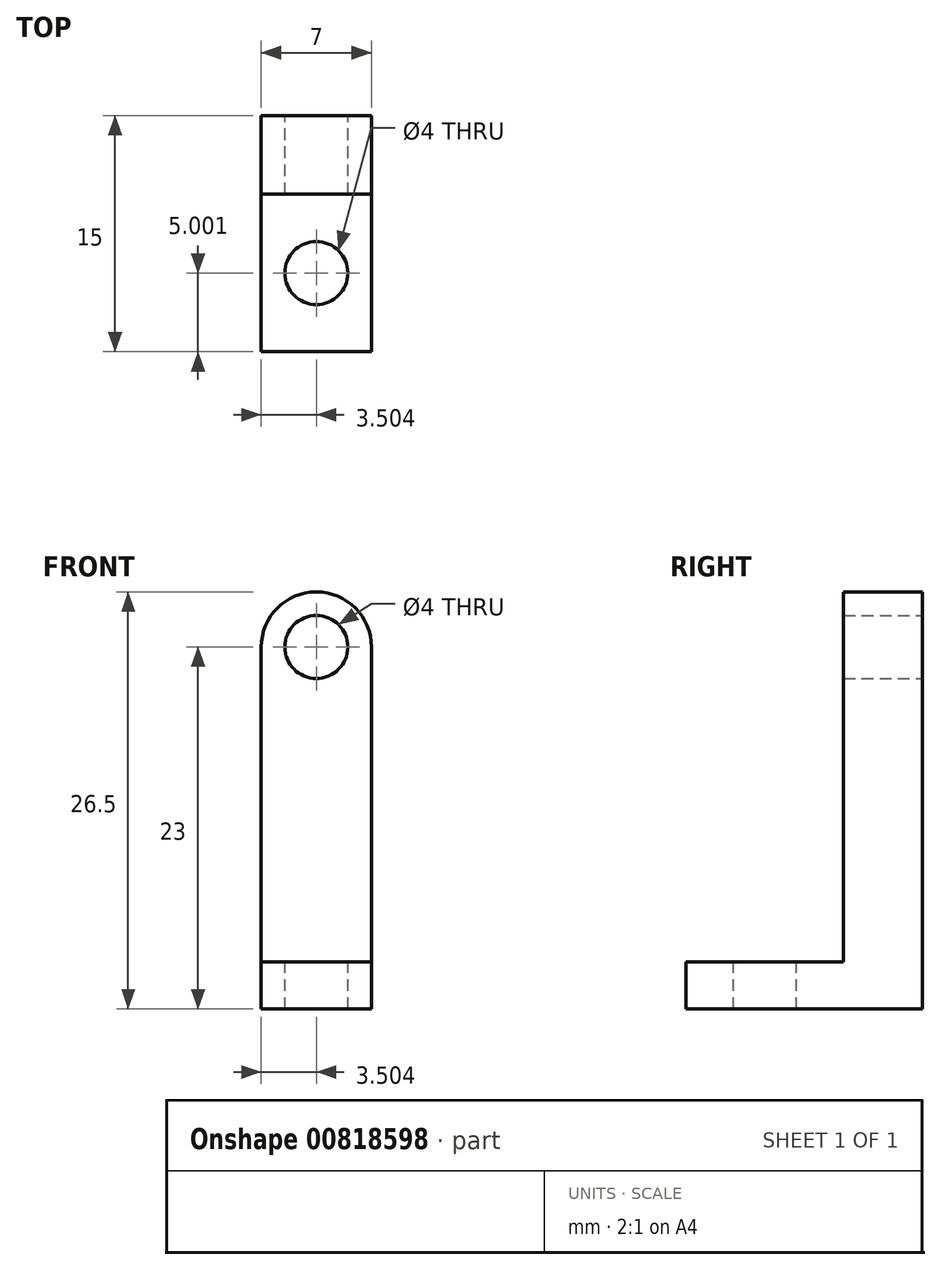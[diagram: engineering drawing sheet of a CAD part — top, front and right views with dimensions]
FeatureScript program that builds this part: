
annotation { "Feature Type Name" : "Feature", "Feature Type Description" : "" }
export const myFeature = defineFeature(function(context is Context, id is Id, definition is map)
    precondition{}
    {
        {
            var Q0;
            Q0=qCreatedBy(makeId("Top.planeOp"),FACE);
            var sketch = newSketch(context, id + "F0", { "sketchPlane" : qUnion([Q0])});
            skLineSegment(sketch, "E0.bottom", {"start": v(-8.2, 9.06) * mm, "end": v(-1.2, 9.06) * mm});
            skLineSegment(sketch, "E0.top", {"start": v(-8.2, -0.94) * mm, "end": v(-1.2, -0.94) * mm});
            skLineSegment(sketch, "E0.left", {"start": v(-8.2, 9.06) * mm, "end": v(-8.2, -0.94) * mm});
            skLineSegment(sketch, "E0.right", {"start": v(-1.2, 9.06) * mm, "end": v(-1.2, -0.94) * mm});
            skLineSegment(sketch, "E1.top", {"start": v(-8.2, 14.06) * mm, "end": v(-1.2, 14.06) * mm});
            skLineSegment(sketch, "E1.left", {"start": v(-8.2, 9.06) * mm, "end": v(-8.2, 14.06) * mm});
            skLineSegment(sketch, "E1.right", {"start": v(-1.2, 9.06) * mm, "end": v(-1.2, 14.06) * mm});
            skSolve(sketch);
        }
        {
            var Q0;
            Q0 = qSketchRegion(id + "F0", true);
            extrude(context, id + "F1", {"entities" : qUnion([Q0]), "depth" : 3 * mm, "offsetDistance" : 25 * mm});
        }
        {
            var Q0;
            Q0=makeQuery(id+"F1.opExtrude","CAP_FACE",FACE,{"disambiguationData":[OSD([sQuery(id+"F0.wireOp",EDGE,"E0.top"),sQuery(id+"F0.wireOp",EDGE,"E0.left"),sQuery(id+"F0.wireOp",EDGE,"E0.right"),sQuery(id+"F0.wireOp",EDGE,"E1.top"),sQuery(id+"F0.wireOp",EDGE,"E1.left"),sQuery(id+"F0.wireOp",EDGE,"E1.right")])],"isStart":false});
            var sketch = newSketch(context, id + "F2", { "sketchPlane" : qUnion([Q0])});
            skLineSegment(sketch, "E2.0", {"start": v(-8.2, 9.06) * mm, "end": v(-1.2, 9.06) * mm});
            skLineSegment(sketch, "E3.0", {"start": v(-8.2, 14.06) * mm, "end": v(-8.2, 9.06) * mm});
            skLineSegment(sketch, "E4.0", {"start": v(-8.2, 14.06) * mm, "end": v(-1.2, 14.06) * mm});
            skLineSegment(sketch, "E5.0", {"start": v(-1.2, 14.06) * mm, "end": v(-1.2, 9.06) * mm});
            skPoint(sketch, "E6.orphan", {"position": v(-8.2, -0.94) * mm});
            skPoint(sketch, "E7.orphan", {"position": v(-1.2, -0.94) * mm});
            skSolve(sketch);
        }
        {
            var Q0;
            Q0 = qSketchRegion(id + "F2", true);
            extrude(context, id + "F3", {"entities" : qUnion([Q0]), "operationType" : NewBodyOperationType.ADD, "depth" : 20 * mm, "offsetDistance" : 25 * mm});
        }
        {
            var Q0;
            Q0=makeQuery(id+"F3.boolean.opBoolean","MERGE",FACE,{"derivedFrom":[makeQuery(id+"F1.opExtrude","SWEPT_FACE",FACE,{"disambiguationData":[OSD([sQuery(id+"F0.wireOp",EDGE,"E1.top")])]}),makeQuery(id+"F3.opExtrude","SWEPT_FACE",FACE,{"disambiguationData":[OSD([sQuery(id+"F2.wireOp",EDGE,"E4.0")])]})]});
            var sketch = newSketch(context, id + "F4", { "sketchPlane" : qUnion([Q0])});
            skLineSegment(sketch, "E8.0", {"start": v(8.2, 23) * mm, "end": v(1.2, 23) * mm});
            skPoint(sketch, "E9", {"position": v(4.7, 23) * mm});
            skArc(sketch, "E10", {"start": v(8.2, 23) * mm, "mid": v(4.7, 26.5) * mm, "end": v(1.2, 23) * mm});
            skSolve(sketch);
        }
        {
            var Q0;
            Q0 = qSketchRegion(id + "F4", true);
            var Q1;
            Q1=makeQuery(id+"F3.opExtrude","SWEPT_FACE",FACE,{"disambiguationData":[OSD([sQuery(id+"F2.wireOp",EDGE,"E2.0")])]});
            extrude(context, id + "F5", {"entities" : qUnion([Q0]), "operationType" : NewBodyOperationType.ADD, "endBound" : BoundingType.UP_TO_SURFACE, "oppositeDirection" : true, "depth" : 25 * mm, "endBoundEntityFace" : qUnion([Q1]), "offsetDistance" : 25 * mm});
        }
        {
            var Q0;
            Q0=makeQuery(id+"F5.boolean.opBoolean","MERGE",FACE,{"derivedFrom":[makeQuery(id+"F3.boolean.opBoolean","MERGE",FACE,{"derivedFrom":[makeQuery(id+"F1.opExtrude","SWEPT_FACE",FACE,{"disambiguationData":[OSD([sQuery(id+"F0.wireOp",EDGE,"E1.top")])]}),makeQuery(id+"F3.opExtrude","SWEPT_FACE",FACE,{"disambiguationData":[OSD([sQuery(id+"F2.wireOp",EDGE,"E4.0")])]})]}),makeQuery(id+"F5.opExtrude","CAP_FACE",FACE,{"disambiguationData":[OSD([sQuery(id+"F4.wireOp",EDGE,"E8.0"),sQuery(id+"F4.wireOp",EDGE,"E10")])],"isStart":true})]});
            var sketch = newSketch(context, id + "F6", { "sketchPlane" : qUnion([Q0])});
            skLineSegment(sketch, "E11", {"start": v(1.2, 23) * mm, "end": v(8.2, 23) * mm, "construction": true});
            skCircle(sketch, "E12", {"center": v(4.7, 23) * mm, "radius": 2 * mm});
            skSolve(sketch);
        }
        {
            var Q0;
            Q0 = qSketchRegion(id + "F6", true);
            extrude(context, id + "F7", {"entities" : qUnion([Q0]), "operationType" : NewBodyOperationType.REMOVE, "endBound" : BoundingType.UP_TO_NEXT, "oppositeDirection" : true, "depth" : 25 * mm, "offsetDistance" : 25 * mm});
        }
        {
            var Q0;
            Q0=makeQuery(id+"F1.opExtrude","CAP_FACE",FACE,{"disambiguationData":[OSD([sQuery(id+"F0.wireOp",EDGE,"E0.top"),sQuery(id+"F0.wireOp",EDGE,"E0.left"),sQuery(id+"F0.wireOp",EDGE,"E0.right"),sQuery(id+"F0.wireOp",EDGE,"E1.top"),sQuery(id+"F0.wireOp",EDGE,"E1.left"),sQuery(id+"F0.wireOp",EDGE,"E1.right")])],"isStart":false});
            var sketch = newSketch(context, id + "F8", { "sketchPlane" : qUnion([Q0])});
            skLineSegment(sketch, "E13", {"start": v(-1.2, 9.06) * mm, "end": v(-8.2, -0.94) * mm, "construction": true});
            skLineSegment(sketch, "E14", {"start": v(-1.2, -0.94) * mm, "end": v(-8.2, 9.06) * mm, "construction": true});
            skPoint(sketch, "E15", {"position": v(-4.7, 4.06) * mm});
            skCircle(sketch, "E16", {"center": v(-4.7, 4.06) * mm, "radius": 2 * mm});
            skSolve(sketch);
        }
        {
            var Q0;
            Q0 = qSketchRegion(id + "F8", true);
            extrude(context, id + "F9", {"entities" : qUnion([Q0]), "operationType" : NewBodyOperationType.REMOVE, "endBound" : BoundingType.UP_TO_NEXT, "oppositeDirection" : true, "depth" : 25 * mm, "offsetDistance" : 25 * mm});
        }
    });
